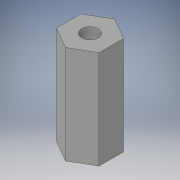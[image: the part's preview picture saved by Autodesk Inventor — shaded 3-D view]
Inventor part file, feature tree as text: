
AUTODESK INVENTOR PART (.ipt)
format: ipt  version: 2018 (Build 220112000, 112)  size: 97,280 bytes
history: native  units: in
note: dims shown in document units (in); Inventor stores cm internally (conversion verified against a paired STEP export)
features: extrude x1, sketch x1
ambient origin geometry x8: Origin, YZ Plane, XZ Plane, XY Plane, X Axis, Y Axis, Z Axis, Center Point
bodies: Solid1 (feature_tree)
feature tree (2):
  extrude  "Extrusion1"  Depth=0.4724in
  sketch  "Sketch1"  dims[d1=0.1181in d2=0.0787in d3=0.4724in d4=0.0in]
